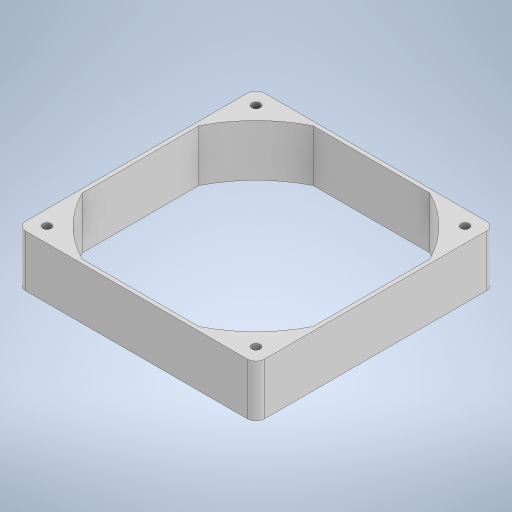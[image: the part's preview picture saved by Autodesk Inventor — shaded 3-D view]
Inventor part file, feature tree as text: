
AUTODESK INVENTOR PART (.ipt)
format: ipt  version: 2023 (Build 270158000, 158)  size: 251,392 bytes
history: native  units: mm
features: extrude x1, fillet x1, sketch x1
ambient origin geometry x8: Origin, YZ Plane, XZ Plane, XY Plane, X Axis, Y Axis, Z Axis, Center Point
bodies: Solid1 (feature_tree)
feature tree (3):
  extrude  "Extrusion1"  Depth=4.233333mm
  fillet  "Fillet1"  Radius=4.233333mm
  sketch  "Sketch1"  dims[d0=120.0mm d1=105.0mm d2=4.233333mm d3=130.0mm d4=2.0mm d5=26.0mm d6=0.0mm d7=4.233333mm]
